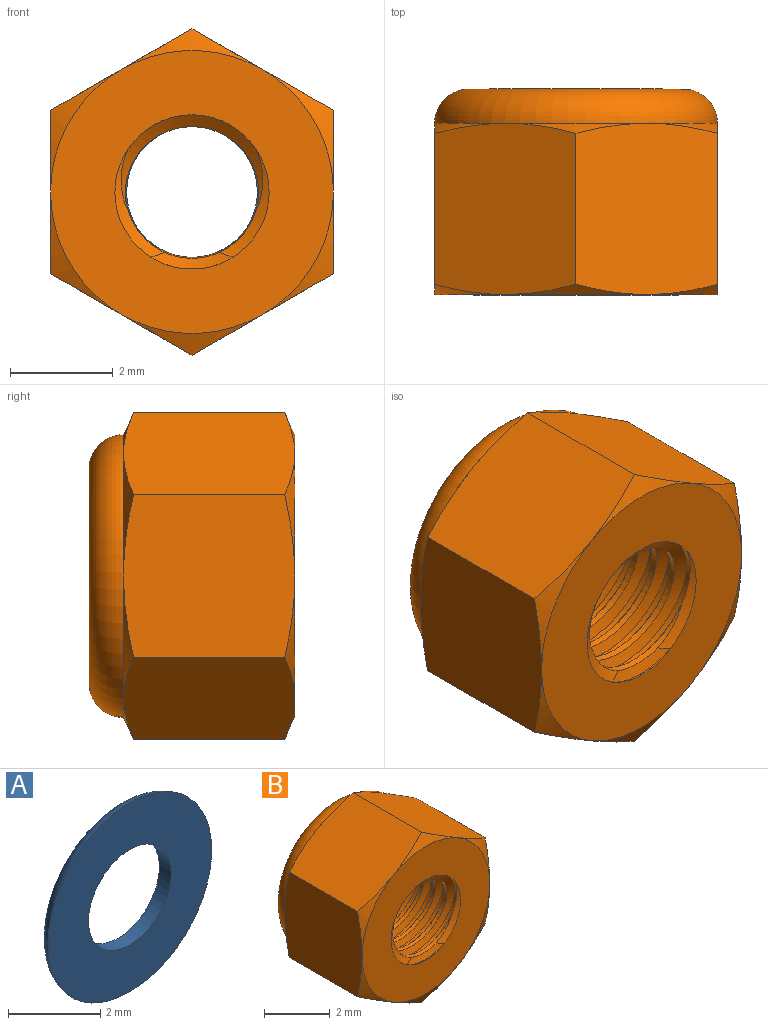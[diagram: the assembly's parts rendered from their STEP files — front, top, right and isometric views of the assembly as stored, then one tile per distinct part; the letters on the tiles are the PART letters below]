
ASSEMBLY  parts=2 mates=1
PART A: 4 faces, bbox 5.5x0.4x5.5 mm
  f0: torus R=2.08mm, axis (0,-1,0), area 9mm2, adj f2,f3
  f1: cylinder r=1.27mm len=2.54mm, axis (0,-1,0), area 2.9mm2, adj f2,f3
  f2: plane 5.03x5.03mm, normal (0,-1,0), area 14.8mm2, adj f0,f1
  f3: plane 4.17x4.17mm, normal (0,1,0), area 8.6mm2, adj f0,f1
PART B: 59 faces, bbox 6.6x4.3x6.6 mm
  f0: cylinder r=1.68mm len=3.35mm, axis (0,-1,0), area 1.6mm2, adj f33,f58
  f1: torus R=2.08mm, axis (0,-1,0), area 12.2mm2, adj f57,f58
  f2: torus R=2.08mm, axis (0,-1,0), area 16.5mm2, adj f3,f33,f46,f47,f48,f49,f50
  f3: cone r=2.75mm half-angle=65deg, axis (0,-1,0), area 0.7mm2, adj f2,f55,f56
  f4: cone r=3.18mm half-angle=65deg, axis (0,1,0), area 0.7mm2, adj f35,f52,f53
  f5: cone r=1.3mm half-angle=60deg, axis (0,-0.99,-0.16), area 2.2mm2, adj f6,f31,f35
  f6: cylinder r=1.3mm len=2.59mm, axis (0,0.99,0.16), area 1mm2, adj f5,f7
  f7: cone r=1.57mm half-angle=60deg, axis (0,0.99,0.16), area 2.3mm2, adj f6,f29
  f8: cone r=1.3mm half-angle=60deg, axis (0,-0.99,-0.16), area 2.3mm2, adj f9,f29
  f9: cylinder r=1.3mm len=2.59mm, axis (0,0.99,0.16), area 1mm2, adj f8,f10
  f10: cone r=1.57mm half-angle=60deg, axis (0,0.99,0.16), area 2.3mm2, adj f9,f28
  f11: cone r=1.3mm half-angle=60deg, axis (0,-0.99,-0.16), area 2.3mm2, adj f12,f28
  f12: cylinder r=1.3mm len=2.59mm, axis (0,0.99,0.16), area 1mm2, adj f11,f13
  f13: cone r=1.57mm half-angle=60deg, axis (0,0.99,0.16), area 2.3mm2, adj f12,f27
  f14: cone r=1.3mm half-angle=60deg, axis (0,-0.99,-0.16), area 2.3mm2, adj f15,f27
  f15: cylinder r=1.3mm len=2.59mm, axis (0,0.99,0.16), area 1mm2, adj f14,f16
  f16: cone r=1.57mm half-angle=60deg, axis (0,0.99,0.16), area 2.3mm2, adj f15,f26
  f17: cone r=1.3mm half-angle=60deg, axis (0,-0.99,-0.16), area 2.3mm2, adj f18,f26
  f18: cylinder r=1.3mm len=2.59mm, axis (0,0.99,0.16), area 1mm2, adj f17,f19
  f19: cone r=1.57mm half-angle=60deg, axis (0,0.99,0.16), area 2.3mm2, adj f18,f25
  f20: cone r=1.3mm half-angle=60deg, axis (0,-0.99,-0.16), area 2.3mm2, adj f21,f25
  f21: cylinder r=1.3mm len=2.59mm, axis (0,0.99,0.16), area 1mm2, adj f20,f22
  f22: cone r=1.57mm half-angle=60deg, axis (0,0.99,0.16), area 2mm2, adj f21,f39,f57
  f23: cylinder r=1.3mm len=2.45mm, axis (0,0.99,0.16), area 0.3mm2, adj f24,f40,f57
  f24: cone r=1.57mm half-angle=60deg, axis (0,0.99,0.16), area 0mm2, adj f23,f57
  f25: cylinder r=1.5mm len=3mm, axis (0,-1,0), area 1.1mm2, adj f19,f20
  f26: cylinder r=1.5mm len=3mm, axis (0,-1,0), area 1.1mm2, adj f16,f17
  f27: cylinder r=1.5mm len=3mm, axis (0,-1,0), area 1.1mm2, adj f13,f14
  f28: cylinder r=1.5mm len=3mm, axis (0,-1,0), area 1.1mm2, adj f10,f11
  f29: cylinder r=1.5mm len=3mm, axis (0,-1,0), area 1.1mm2, adj f7,f8
  f30: cylinder r=1.5mm len=1.6mm, axis (0,-1,0), area 0mm2, adj f32,f35
  f31: cylinder r=1.5mm len=3mm, axis (0,-1,0), area 1.1mm2, adj f5,f35,f37
  f32: cone r=1.3mm half-angle=60deg, axis (0,-0.99,-0.16), area 0.3mm2, adj f30,f34,f36,f38
  f33: plane 4.17x4.17mm, normal (0,1,0), area 4.8mm2, adj f0,f2
  f34: cone r=1.5mm half-angle=65deg, axis (0,-1,0), area 0.4mm2, adj f32,f35,f37,f38
  f35: plane 5.5x5.5mm, normal (0,-1,0), area 16.7mm2, adj f4,f5,f30,f31,f34,f36,f41,f42
  f36: cone r=1.5mm half-angle=65deg, axis (0,-1,0), area 0.4mm2, adj f32,f35,f37,f38
  f37: cone r=1.57mm half-angle=60deg, axis (0,0.99,0.16), area 1.3mm2, adj f31,f34,f36,f38
  f38: cylinder r=1.3mm len=2.45mm, axis (0,0.99,0.16), area 0.3mm2, adj f32,f34,f36,f37
  f39: cylinder r=1.5mm len=3mm, axis (0,-1,0), area 1.5mm2, adj f22,f40,f57
  f40: cone r=1.3mm half-angle=60deg, axis (0,-0.99,-0.16), area 1mm2, adj f23,f39,f57
  f41: cone r=3.18mm half-angle=65deg, axis (0,1,0), area 0.7mm2, adj f35,f51,f52
  f42: cone r=3.18mm half-angle=65deg, axis (0,1,0), area 0.7mm2, adj f35,f51,f56
  f43: cone r=3.18mm half-angle=65deg, axis (0,1,0), area 0.7mm2, adj f35,f55,f56
  f44: cone r=3.18mm half-angle=65deg, axis (0,1,0), area 0.7mm2, adj f35,f54,f55
  f45: cone r=3.18mm half-angle=65deg, axis (0,1,0), area 0.7mm2, adj f35,f53,f54
  f46: cone r=2.75mm half-angle=65deg, axis (0,-1,0), area 0.7mm2, adj f2,f53,f54
  f47: cone r=2.75mm half-angle=65deg, axis (0,-1,0), area 0.7mm2, adj f2,f54,f55
  f48: cone r=2.75mm half-angle=65deg, axis (0,-1,0), area 0.7mm2, adj f2,f52,f53
  f49: cone r=2.75mm half-angle=65deg, axis (0,-1,0), area 0.7mm2, adj f2,f51,f56
  f50: cone r=2.75mm half-angle=65deg, axis (0,-1,0), area 0.7mm2, adj f2,f51,f52
  f51: plane 3.58x3.43mm, normal (1,0,0), area 10.2mm2, adj f41,f42,f49,f50,f52,f56
  f52: plane 3.58x2.99mm, normal (0.5,0,0.87), area 10.1mm2, adj f4,f41,f48,f50,f51,f53
  f53: plane 3.58x2.99mm, normal (-0.5,0,0.87), area 10.1mm2, adj f4,f45,f46,f48,f52,f54
  f54: plane 3.58x3.43mm, normal (-1,0,0), area 10.2mm2, adj f44,f45,f46,f47,f53,f55
  f55: plane 3.58x2.99mm, normal (-0.5,0,-0.87), area 10.1mm2, adj f3,f43,f44,f47,f54,f56
  f56: plane 3.58x2.99mm, normal (0.5,0,-0.87), area 10.1mm2, adj f3,f42,f43,f49,f51,f55
  f57: plane 5.26x5.26mm, normal (0,1,0), area 15.2mm2, adj f1,f22,f23,f24,f39,f40
  f58: plane 4.17x4.17mm, normal (0,-1,0), area 4.8mm2, adj f0,f1
PLACE A t=(60.7,61.95,55.54)mm
PLACE B t=(60.7,61.92,55.54)mm
MATE fastened A.f0 <-> B.f1  axis (0,-1,0) through (60.7,65.62,55.54)mm
